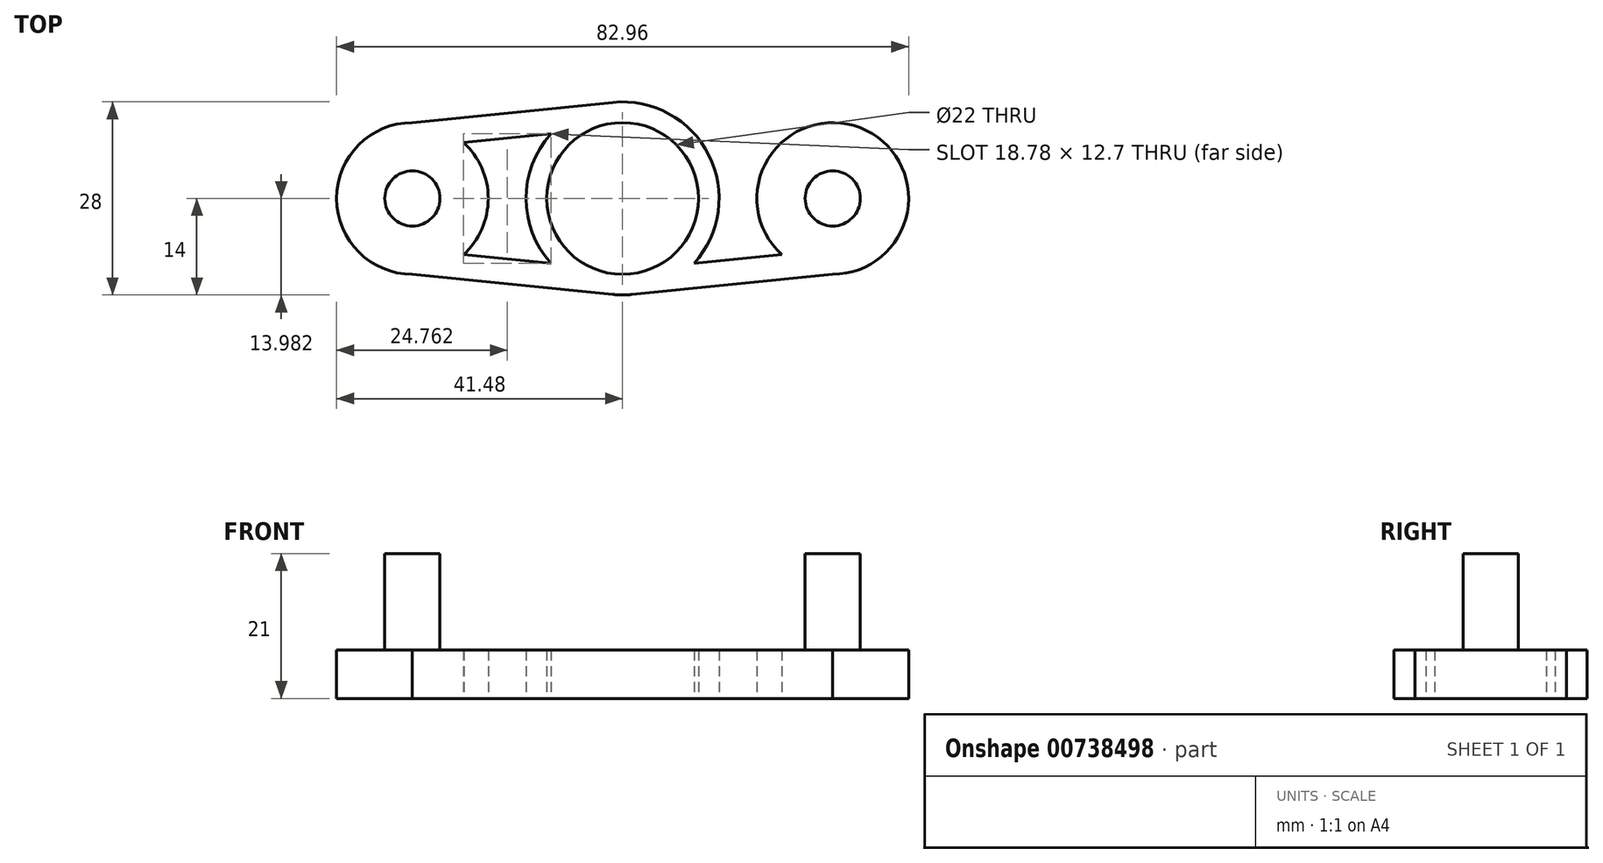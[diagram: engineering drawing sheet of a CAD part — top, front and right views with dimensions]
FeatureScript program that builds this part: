
annotation { "Feature Type Name" : "Feature", "Feature Type Description" : "" }
export const myFeature = defineFeature(function(context is Context, id is Id, definition is map)
    precondition{}
    {
        {
            var Q0;
            Q0=qCreatedBy(makeId("Top.planeOp"),FACE);
            var sketch = newSketch(context, id + "F0", { "sketchPlane" : qUnion([Q0])});
            skCircle(sketch, "E0", {"center": v(0, 0) * mm, "radius": 11 * mm});
            skCircle(sketch, "E1", {"center": v(-30.48, 0) * mm, "radius": 11 * mm});
            skCircle(sketch, "E2", {"center": v(30.48, 0) * mm, "radius": 11 * mm});
            skCircle(sketch, "E3", {"center": v(0, 0) * mm, "radius": 14 * mm});
            skLineSegment(sketch, "E4", {"start": v(-30.48, -11) * mm, "end": v(0, -14.07) * mm});
            skLineSegment(sketch, "E5", {"start": v(0, -14.07) * mm, "end": v(30.48, -11) * mm});
            skLineSegment(sketch, "E6", {"start": v(-30.48, 11) * mm, "end": v(0, 14.07) * mm});
            skLineSegment(sketch, "E7", {"start": v(-23.04, 8.1) * mm, "end": v(-10.4, 9.37) * mm});
            skLineSegment(sketch, "E8", {"start": v(-23.07, -8.13) * mm, "end": v(-10.37, -9.4) * mm});
            skLineSegment(sketch, "E9", {"start": v(10.37, -9.4) * mm, "end": v(23.07, -8.13) * mm});
            skLineSegment(sketch, "E10", {"start": v(30.48, 11) * mm, "end": v(0, 14.07) * mm});
            skLineSegment(sketch, "E11", {"start": v(10.4, 9.37) * mm, "end": v(23.04, 8.1) * mm});
            skLineSegment(sketch, "E12", {"start": v(23.04, 8.1) * mm, "end": v(10.4, 9.37) * mm});
            skCircle(sketch, "E13", {"center": v(-30.48, 0) * mm, "radius": 4 * mm});
            skCircle(sketch, "E14", {"center": v(30.48, 0) * mm, "radius": 4 * mm});
            skSolve(sketch);
        }
        {
            var Q0;
            {var subQ0=sQuery(id+"F0.wireOp",EDGE,"E1");var subQ1=makeQuery(id+"F0.imprint","INTERSECT",VERTEX,{"derivedFrom":[subQ0,sQuery(id+"F0.wireOp",EDGE,"E6")]});Q0=makeQuery(id+"F0.imprint","IMPRINT",FACE,{"disambiguationData":[TD([[makeQuery(id+"F0.imprint","IMPRINT",EDGE,{"disambiguationData":[TD([[subQ1,1.0]])],"derivedFrom":subQ0}),1.0]])]});}
            var Q1;
            {var subQ3=sQuery(id+"F0.wireOp",EDGE,"E8");Q1=makeQuery(id+"F0.imprint","IMPRINT",FACE,{"disambiguationData":[TD([[makeQuery(id+"F0.imprint","IMPRINT",EDGE,{"derivedFrom":subQ3}),-1.0]])]});}
            var Q2;
            Q2=makeQuery(id+"F0.imprint","IMPRINT",FACE,{"disambiguationData":[TD([[makeQuery(id+"F0.imprint","IMPRINT",EDGE,{"derivedFrom":sQuery(id+"F0.wireOp",EDGE,"E0")}),-1.0]])]});
            var Q3;
            {var subQ3=sQuery(id+"F0.wireOp",EDGE,"E9");Q3=makeQuery(id+"F0.imprint","IMPRINT",FACE,{"disambiguationData":[TD([[makeQuery(id+"F0.imprint","IMPRINT",EDGE,{"derivedFrom":subQ3}),-1.0]])]});}
            var Q4;
            {var subQ0=sQuery(id+"F0.wireOp",EDGE,"E2");var subQ1=makeQuery(id+"F0.imprint","INTERSECT",VERTEX,{"derivedFrom":[subQ0,sQuery(id+"F0.wireOp",EDGE,"E10")]});Q4=makeQuery(id+"F0.imprint","IMPRINT",FACE,{"disambiguationData":[TD([[makeQuery(id+"F0.imprint","IMPRINT",EDGE,{"disambiguationData":[TD([[subQ1,-1.0]])],"derivedFrom":subQ0}),1.0]])]});}
            var Q5;
            {var subQ3=sQuery(id+"F0.wireOp",EDGE,"E12");Q5=makeQuery(id+"F0.imprint","IMPRINT",FACE,{"disambiguationData":[TD([[makeQuery(id+"F0.imprint","IMPRINT",EDGE,{"derivedFrom":subQ3}),-1.0]])]});}
            var Q6;
            {var subQ3=sQuery(id+"F0.wireOp",EDGE,"E7");Q6=makeQuery(id+"F0.imprint","IMPRINT",FACE,{"disambiguationData":[TD([[makeQuery(id+"F0.imprint","IMPRINT",EDGE,{"derivedFrom":subQ3}),1.0]])]});}
            extrude(context, id + "F1", {"entities" : qUnion([Q0, Q1, Q2, Q3, Q4, Q5, Q6]), "flatOperationType" : FlatOperationType.REMOVE, "depth" : 7 * mm, "offsetDistance" : 25.4 * mm, "domain" : OperationDomain.MODEL});
        }
        {
            var Q0;
            Q0=makeQuery(id+"F0.imprint","IMPRINT",FACE,{"disambiguationData":[TD([[makeQuery(id+"F0.imprint","IMPRINT",EDGE,{"derivedFrom":sQuery(id+"F0.wireOp",EDGE,"E13")}),1.0]])]});
            var Q1;
            Q1=makeQuery(id+"F0.imprint","IMPRINT",FACE,{"disambiguationData":[TD([[makeQuery(id+"F0.imprint","IMPRINT",EDGE,{"derivedFrom":sQuery(id+"F0.wireOp",EDGE,"E14")}),1.0]])]});
            extrude(context, id + "F2", {"entities" : qUnion([Q0, Q1]), "operationType" : NewBodyOperationType.ADD, "flatOperationType" : FlatOperationType.REMOVE, "depth" : 21 * mm, "offsetDistance" : 25.4 * mm, "domain" : OperationDomain.MODEL});
        }
    });
